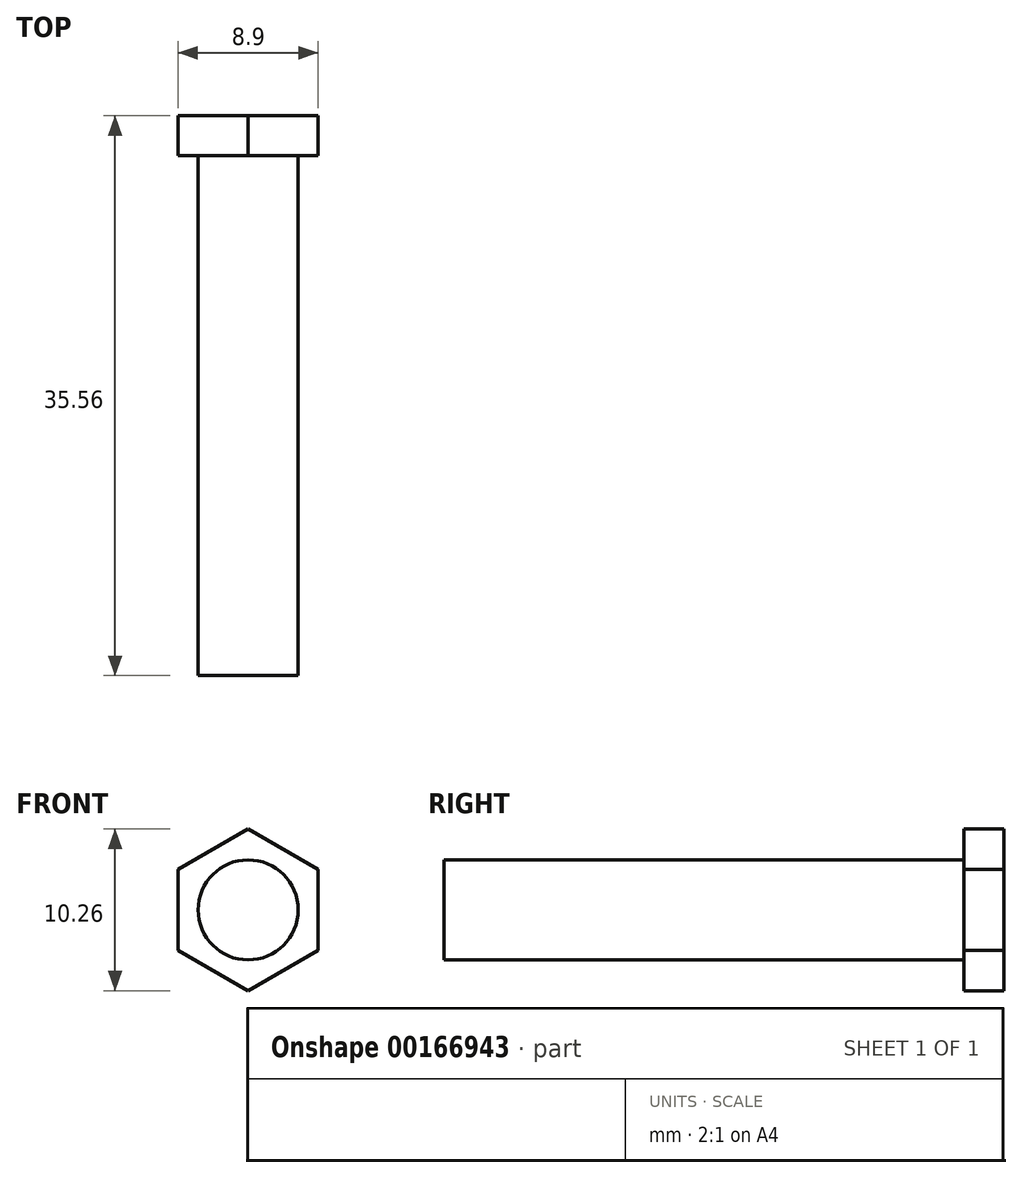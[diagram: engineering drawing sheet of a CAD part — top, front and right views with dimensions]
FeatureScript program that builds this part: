
annotation { "Feature Type Name" : "Feature", "Feature Type Description" : "" }
export const myFeature = defineFeature(function(context is Context, id is Id, definition is map)
    precondition{}
    {
        {
            var Q0;
            Q0=qCreatedBy(makeId("Front.planeOp"),FACE);
            var sketch = newSketch(context, id + "F0", { "sketchPlane" : qUnion([Q0])});
            skCircle(sketch, "E0", {"center": v(0, 0) * mm, "radius": 3.18 * mm});
            skSolve(sketch);
        }
        {
            var Q0;
            Q0 = qSketchRegion(id + "F0", true);
            extrude(context, id + "F1", {"entities" : qUnion([Q0]), "depth" : 33.02 * mm});
        }
        {
            var Q0;
            Q0=makeQuery(id+"F1.opExtrude","CAP_FACE",FACE,{"disambiguationData":[OSD([sQuery(id+"F0.wireOp",EDGE,"E0")])],"isStart":true});
            var sketch = newSketch(context, id + "F2", { "sketchPlane" : qUnion([Q0])});
            skCircle(sketch, "E1.cCircle", {"center": v(0, 0) * mm, "radius": 4.45 * mm, "construction": true});
            skLineSegment(sketch, "E1.0", {"start": v(4.45, 2.57) * mm, "end": v(4.45, -2.57) * mm});
            skLineSegment(sketch, "E1.1", {"start": v(4.45, -2.57) * mm, "end": v(0, -5.13) * mm});
            skLineSegment(sketch, "E1.2", {"start": v(0, -5.13) * mm, "end": v(-4.44, -2.57) * mm});
            skLineSegment(sketch, "E1.3", {"start": v(-4.44, -2.57) * mm, "end": v(-4.45, 2.57) * mm});
            skLineSegment(sketch, "E1.4", {"start": v(-4.45, 2.57) * mm, "end": v(0, 5.13) * mm});
            skLineSegment(sketch, "E1.5", {"start": v(0, 5.13) * mm, "end": v(4.44, 2.57) * mm});
            skPoint(sketch, "E1.0.midPoint", {"position": v(4.45, 0) * mm});
            skSolve(sketch);
        }
        {
            var Q0;
            Q0 = qSketchRegion(id + "F2", true);
            extrude(context, id + "F3", {"entities" : qUnion([Q0]), "operationType" : NewBodyOperationType.ADD, "depth" : 2.54 * mm});
        }
    });
